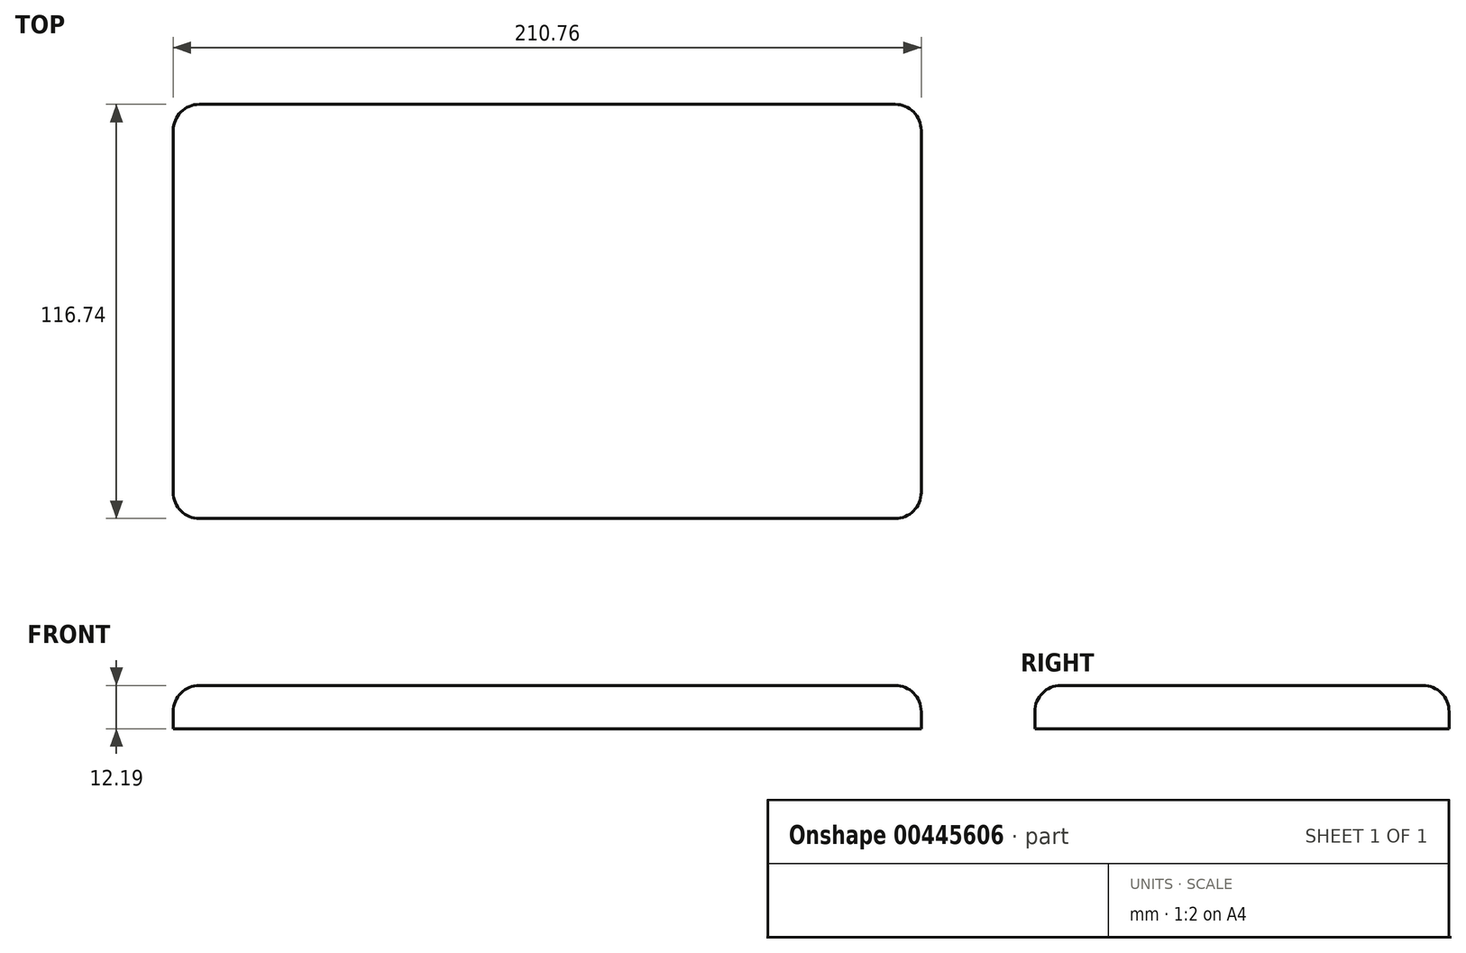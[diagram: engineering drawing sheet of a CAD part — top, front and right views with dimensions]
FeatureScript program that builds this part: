
annotation { "Feature Type Name" : "Feature", "Feature Type Description" : "" }
export const myFeature = defineFeature(function(context is Context, id is Id, definition is map)
    precondition{}
    {
        {
            var Q0;
            Q0=qCreatedBy(makeId("Top.planeOp"),FACE);
            var sketch = newSketch(context, id + "F0", { "sketchPlane" : qUnion([Q0])});
            skLineSegment(sketch, "E0.bottom", {"start": v(-105.38, 58.37) * mm, "end": v(105.38, 58.37) * mm});
            skLineSegment(sketch, "E0.top", {"start": v(-105.38, -58.37) * mm, "end": v(105.38, -58.37) * mm});
            skLineSegment(sketch, "E0.left", {"start": v(-105.38, 58.37) * mm, "end": v(-105.38, -58.37) * mm});
            skLineSegment(sketch, "E0.right", {"start": v(105.38, 58.37) * mm, "end": v(105.38, -58.37) * mm});
            skPoint(sketch, "E0.middle", {"position": v(0, 0) * mm});
            skSolve(sketch);
        }
        {
            var Q0;
            Q0=makeQuery(id+"F0.imprint","IMPRINT",FACE,{"disambiguationData":[TD([[makeQuery(id+"F0.imprint","IMPRINT",EDGE,{"derivedFrom":sQuery(id+"F0.wireOp",EDGE,"E0.bottom")}),-1.0]])]});
            extrude(context, id + "F1", {"entities" : qUnion([Q0]), "depth" : 12.2 * mm});
        }
        {
            var Q0;
            Q0=makeQuery(id+"F1.opExtrude","CAP_EDGE",EDGE,{"disambiguationData":[OSD([sQuery(id+"F0.wireOp",EDGE,"E0.top")])],"isStart":false});
            var Q1;
            Q1=makeQuery(id+"F1.opExtrude","CAP_EDGE",EDGE,{"disambiguationData":[OSD([sQuery(id+"F0.wireOp",EDGE,"E0.right")])],"isStart":false});
            var Q2;
            Q2=makeQuery(id+"F1.opExtrude","CAP_EDGE",EDGE,{"disambiguationData":[OSD([sQuery(id+"F0.wireOp",EDGE,"E0.bottom")])],"isStart":false});
            var Q3;
            Q3=makeQuery(id+"F1.opExtrude","CAP_EDGE",EDGE,{"disambiguationData":[OSD([sQuery(id+"F0.wireOp",EDGE,"E0.left")])],"isStart":false});
            var Q4;
            Q4=makeQuery(id+"F1.opExtrude","SWEPT_EDGE",EDGE,{"disambiguationData":[OSD([sQuery(id+"F0.wireOp",EDGE,"E0.top"),sQuery(id+"F0.wireOp",EDGE,"E0.right")])]});
            var Q5;
            Q5=makeQuery(id+"F1.opExtrude","SWEPT_EDGE",EDGE,{"disambiguationData":[OSD([sQuery(id+"F0.wireOp",EDGE,"E0.bottom"),sQuery(id+"F0.wireOp",EDGE,"E0.right")])]});
            var Q6;
            Q6=makeQuery(id+"F1.opExtrude","SWEPT_EDGE",EDGE,{"disambiguationData":[OSD([sQuery(id+"F0.wireOp",EDGE,"E0.top"),sQuery(id+"F0.wireOp",EDGE,"E0.left")])]});
            var Q7;
            Q7=makeQuery(id+"F1.opExtrude","CAP_FACE",FACE,{"disambiguationData":[OSD([sQuery(id+"F0.wireOp",EDGE,"E0.bottom"),sQuery(id+"F0.wireOp",EDGE,"E0.top"),sQuery(id+"F0.wireOp",EDGE,"E0.left"),sQuery(id+"F0.wireOp",EDGE,"E0.right")])],"isStart":false});
            var Q8;
            Q8=makeQuery(id+"F1.opExtrude","SWEPT_EDGE",EDGE,{"disambiguationData":[OSD([sQuery(id+"F0.wireOp",EDGE,"E0.bottom"),sQuery(id+"F0.wireOp",EDGE,"E0.left")])]});
            fillet(context, id + "F2", {"entities" : qUnion([Q0, Q1, Q2, Q3, Q4, Q5, Q6, Q7, Q8]), "radius" : 7.36 * mm, "tangentPropagation" : true, "allowEdgeOverflow" : false});
        }
    });
